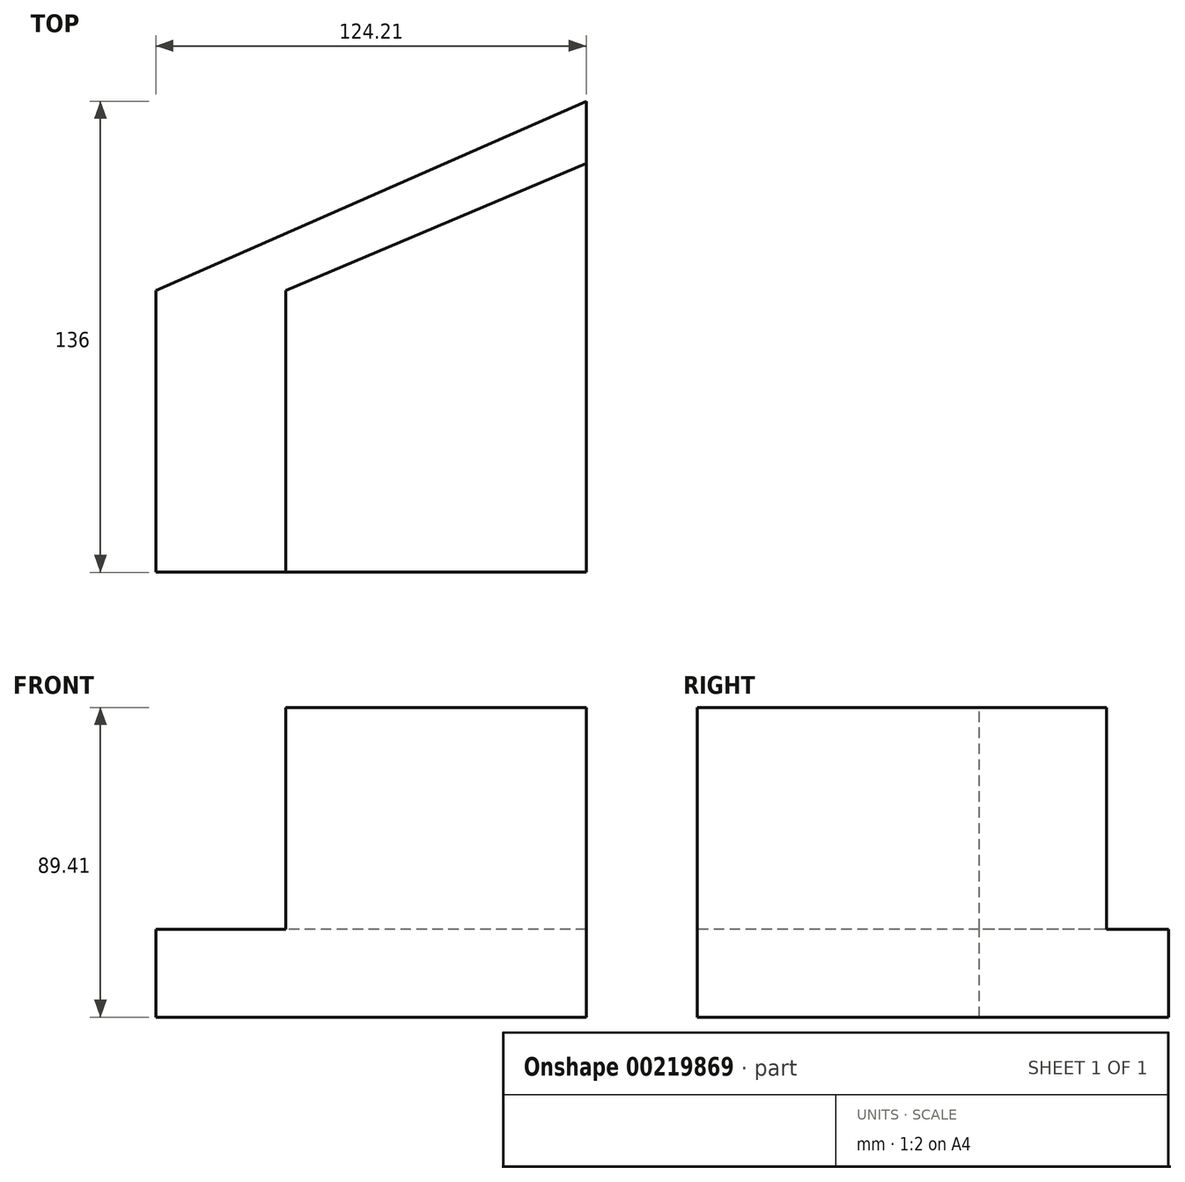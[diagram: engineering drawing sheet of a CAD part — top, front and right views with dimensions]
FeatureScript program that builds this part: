
annotation { "Feature Type Name" : "Feature", "Feature Type Description" : "" }
export const myFeature = defineFeature(function(context is Context, id is Id, definition is map)
    precondition{}
    {
        {
            var Q0;
            Q0=qCreatedBy(makeId("Top.planeOp"),FACE);
            var sketch = newSketch(context, id + "F0", { "sketchPlane" : qUnion([Q0])});
            skLineSegment(sketch, "E0.top", {"start": v(-43.4, -59.04) * mm, "end": v(43.4, -59.04) * mm});
            skLineSegment(sketch, "E0.left", {"start": v(-43.4, 22.35) * mm, "end": v(-43.4, -59.04) * mm});
            skLineSegment(sketch, "E0.right", {"start": v(43.4, 59.04) * mm, "end": v(43.4, -59.04) * mm});
            skPoint(sketch, "E0.middle", {"position": v(0, 0) * mm});
            skLineSegment(sketch, "E1", {"start": v(43.4, 59.04) * mm, "end": v(-43.4, 22.35) * mm});
            skPoint(sketch, "E0.bottom.start.orphan", {"position": v(-43.4, 59.04) * mm});
            skSolve(sketch);
        }
        {
            var Q0;
            Q0 = qSketchRegion(id + "F0", true);
            extrude(context, id + "F1", {"entities" : qUnion([Q0]), "oppositeDirection" : true, "depth" : 64 * mm});
        }
        {
            var Q0;
            Q0=makeQuery(id+"F1.opExtrude","CAP_FACE",FACE,{"disambiguationData":[OSD([sQuery(id+"F0.wireOp",EDGE,"E0.top"),sQuery(id+"F0.wireOp",EDGE,"E0.left"),sQuery(id+"F0.wireOp",EDGE,"E0.right"),sQuery(id+"F0.wireOp",EDGE,"E1")])],"isStart":false});
            var sketch = newSketch(context, id + "F2", { "sketchPlane" : qUnion([Q0])});
            skLineSegment(sketch, "E2", {"start": v(-43.4, -22.35) * mm, "end": v(-80.82, -22.35) * mm});
            skLineSegment(sketch, "E3", {"start": v(-80.82, -22.35) * mm, "end": v(-80.82, 59.04) * mm});
            skLineSegment(sketch, "E4", {"start": v(-80.82, 59.04) * mm, "end": v(-43.4, 59.04) * mm});
            skLineSegment(sketch, "E5", {"start": v(43.4, -59.04) * mm, "end": v(43.4, -76.96) * mm});
            skLineSegment(sketch, "E6", {"start": v(43.4, -76.96) * mm, "end": v(-80.82, -22.35) * mm});
            skSolve(sketch);
        }
        {
            var Q0;
            Q0 = qSketchRegion(id + "F2", true);
            var Q1;
            Q1=makeQuery(id+"F2.imprint","IMPRINT",FACE,{"disambiguationData":[TD([[makeQuery(id+"F2.imprint","IMPRINT",EDGE,{"derivedFrom":sQuery(id+"F2.wireOp",EDGE,"E2")}),-1.0]])]});
            var Q2;
            Q2=makeQuery(id+"F2.imprint","IMPRINT",FACE,{"disambiguationData":[TD([[makeQuery(id+"F2.imprint","IMPRINT",EDGE,{"derivedFrom":sQuery(id+"F2.wireOp",EDGE,"E2")}),1.0]])]});
            var Q3;
            Q3=makeQuery(id+"F2.imprint","IMPRINT",FACE,{"disambiguationData":[TD([[makeQuery(id+"F2.imprint","IMPRINT",EDGE,{"derivedFrom":makeQuery(id+"F1.opExtrude","CAP_EDGE",EDGE,{"disambiguationData":[OSD([sQuery(id+"F0.wireOp",EDGE,"E0.top")])],"isStart":false})}),-1.0]])]});
            extrude(context, id + "F3", {"entities" : qUnion([Q0, Q1, Q2, Q3]), "operationType" : NewBodyOperationType.ADD, "depth" : 25.4 * mm});
        }
    });
